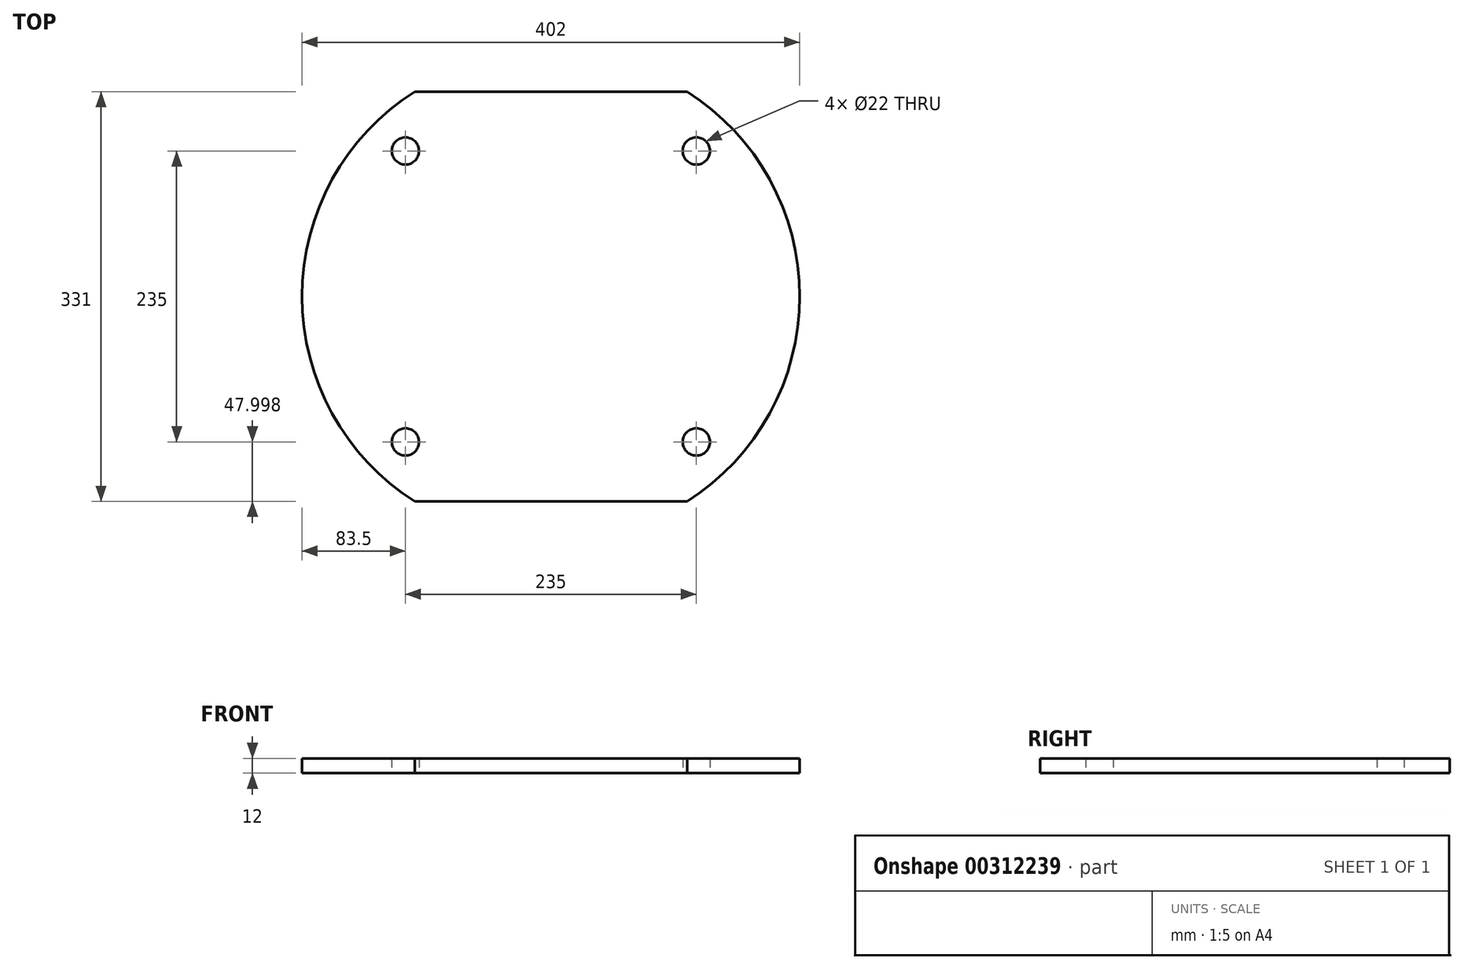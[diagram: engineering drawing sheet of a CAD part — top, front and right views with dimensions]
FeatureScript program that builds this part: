
annotation { "Feature Type Name" : "Feature", "Feature Type Description" : "" }
export const myFeature = defineFeature(function(context is Context, id is Id, definition is map)
    precondition{}
    {
        {
            var Q0;
            Q0=qCreatedBy(makeId("Top.planeOp"),FACE);
            var sketch = newSketch(context, id + "F0", { "sketchPlane" : qUnion([Q0])});
            skLineSegment(sketch, "E0", {"start": v(-110, 165.5) * mm, "end": v(110, 165.5) * mm});
            skLineSegment(sketch, "E1", {"start": v(110, -165.5) * mm, "end": v(-110, -165.5) * mm});
            skArc(sketch, "E2", {"start": v(-110, 165.5) * mm, "mid": v(-201, 0) * mm, "end": v(-110, -165.5) * mm});
            skArc(sketch, "E3", {"start": v(110, -165.5) * mm, "mid": v(201, 0) * mm, "end": v(110, 165.5) * mm});
            skCircle(sketch, "E4", {"center": v(-117.5, -117.5) * mm, "radius": 11 * mm});
            skCircle(sketch, "E5", {"center": v(117.5, -117.5) * mm, "radius": 11 * mm});
            skCircle(sketch, "E6", {"center": v(117.5, 117.5) * mm, "radius": 11 * mm});
            skCircle(sketch, "E7", {"center": v(-117.5, 117.5) * mm, "radius": 11 * mm});
            skPoint(sketch, "E8.startSnap0", {"position": v(-201, 0) * mm});
            skPoint(sketch, "E9.startSnap0", {"position": v(201, 0) * mm});
            skSolve(sketch);
        }
        {
            var Q0;
            Q0 = qSketchRegion(id + "F0", true);
            extrude(context, id + "F1", {"entities" : qUnion([Q0]), "depth" : 12 * mm, "offsetDistance" : 25 * mm});
        }
    });
